# Revit family: R-MMA-480
name_source: partatom
category: Portes
units: mm (PartAtom-declared; Revit-internal decimal feet)

## family parameters
Couper avec des vides une fois chargée = Non
Hôte = Mur
Partagée = Non
Point de calcul de pièce = Oui
Toujours verticalement = Oui

## types (1)
- R-MMA-480
    ----- EQUIPEMENTS ----------------------- = .
    ----- PARAMETRES DE L'HÔTE -------------------- = .
    ----- PARAMETRES DES VANTAUX -------------------- = .
    ----- PARAMETRES POSITION HUISSERIE -------------------- = .
    ----- PARAMETRES PROFIL HUISSERIE -------------------- = .
    ----- TYPE D'HUISSERIE -------------------- = .
    ----- TYPE DE VANTAIL -------------------- = .
    ----PARAMETRES INUTILISES------------------------- = .
    1 Vantail = Oui
    2 Vantaux = Non
    A.E.V = A*4.E*7B.V*C4
    Acoustique = Rw (C ; Ctr) = 43(-1 ;-4)
    Certification = PEFC
    Coloris Oculus = Lauan - Meranti
    Coloris Oculus Métal = Acier - finition peinture thermolaque - gris - brillant
    Coloris Verre Oculus = Verre
    Coloris_Chants = Prépeint
    Construction analytique = <Aucun>
    DAS = Non
    Description = MPC43 COURSIVE - REPRISE DE DOUBLAGE - HB
    Décalage Largeur Paumelle Recouvrement = 0 mm  [stored 0 ft]
    Décalage_Seuil_Vantail = 0 mm  [stored 0 ft]
    Désaffleurement_Vantail = 0 mm  [stored 0 ft]
    Epaisseurs_Vantaux = 58 mm  [stored 0.190289 ft]
    Espacement_Paumelle_Vantail = 0 mm  [stored 0 ft]
    Fabricant = MALERBA
    Ferrage_Encastre = Non
    Fiche Moati = Oui
    Fiche_Produit = MMA-480
    Gabarit_VR = 6
    Hauteur Feuillure Basse Vantail = 18 mm  [stored 0.0590551 ft]
    Hauteur_Axe_Bequille = 1045 mm  [stored 3.42848 ft]
    Hauteur_Vantaux_Souhaitée = 2147 mm  [stored 7.04396 ft]
    Ht Microviseur = 1500 mm  [stored 4.92126 ft]
    Inv_Espacement_Paumelle_Vantail = 5 mm  [stored 0.0164042 ft]
    Inv_Position_Largeur_Paumelle = 0 mm  [stored 0 ft]
    Jeu Profondeur Recouvrement Vantail = 0 mm  [stored 0 ft]
    Jeu_Côté_Articulation_Vantail = 6 mm  [stored 0.019685 ft]
    Jeu_Côté_Fermeture_Vantail = 4 mm  [stored 0.0131234 ft]
    Jeu_Traverse_Basse_Vantail = 8 mm  [stored 0.0262467 ft]
    Jeu_Traverse_Haute_Vantail = 0 mm  [stored 0 ft]
    Largeur Feuillure Battement Articulation = 18 mm  [stored 0.0590551 ft]
    Largeur_Axe_Bequille = 60 mm  [stored 0.19685 ft]
    Largeur_Feuillure_Battement_Semi_Fixe = 18 mm  [stored 0.0590551 ft]
    Largeur_Feuillure_Battement_Service = 18 mm  [stored 0.0590551 ft]
    Largeur_Feuillure_Profil = 18 mm  [stored 0.0590551 ft]
    Largeur_Vantail_Semi_Fixe_Souhaitée = 630 mm  [stored 2.06693 ft]
    Largeur_Vantail_Service_Souhaitée = 960 mm  [stored 3.14961 ft]
    Materiaux_Dominant = Métal
    Microviseur = Non
    Modèle = 43 - SA-HB
    Note d'identification = Bloc-porte métal palier coursive MPC43 1 vantail, simple action, EI30, 43(-1; -4) dB, 1,3 W/m².K, A*4.E*7B.V*C4, stabilité garantie, pour montage reprise de doublage, sur huisserie bois
    Paumelle = Non
    Paumelle_1 = 230 mm  [stored 0.754593 ft]
    Paumelle_2 = 859 mm  [stored 2.81824 ft]
    Paumelle_3 = 859 mm  [stored 2.81824 ft]
    Paumelle_4 = 165 mm
    Pivot_PMT = Non
    Position_Largeur_Paumelle = 0 mm  [stored 0 ft]
    Profondeur Feuillure Basse Vantail = 43 mm  [stored 0.141076 ft]
    Profondeur Feuillure Battement Articulation = 43 mm  [stored 0.141076 ft]
    Profondeur_Feuillure_Battement_Semi_Fixe = 15 mm  [stored 0.0492126 ft]
    Profondeur_Feuillure_Battement_Service = 43 mm  [stored 0.141076 ft]
    Profondeur_Feuillure_Profil = 43 mm  [stored 0.141076 ft]
    Reference_Commerciale = MPC43 EXTERIEUR
    Reprise_Doublage_1 = 30 mm  [stored 0.0984252 ft]
    Reprise_Doublage_2 = 30 mm  [stored 0.0984252 ft]
    Reprise_Doublage_Haut = 30 mm  [stored 0.0984252 ft]
    Resistance_Feu = EI30
    Schéma de simplification = S10
    Sens_Feu = Coté fiches
    Stabilité = Garantie
    Thermique (W/m2.°K) = 1.3
    URL = https://www.malerba.fr
    Vantail à Recouvrement = Oui
    Visibilite_Paum-4 = Oui
    Visibilite_Poignee = Oui
    X_Décalage Hauteur Feuillure Recouvrement = 18 mm  [stored 0.0590551 ft]
    X_Décalage Largeur Feuillure Recouvrement = 36 mm
    X_Décalage Largeur Recouvrement Vantail = 18 mm  [stored 0.0590551 ft]
    X_Décalage Profondeur Recouvrement Vantail = 15 mm  [stored 0.0492126 ft]
    X_Espacement_Paumelle_Vantail = 0 mm  [stored 0 ft]
    X_Fiche Moati = Oui
    X_Inv Décalage Profondeur Recouvrement Vantail = 5 mm  [stored 0.0164042 ft]
    X_Inv_Espacement_Paumelle_Vantail = 5 mm  [stored 0.0164042 ft]
    X_Inv_Position_Largeur_Paumelle = 0 mm  [stored 0 ft]
    X_Paumelle = Non

note: [stored X ft] marks values corroborated as IEEE doubles in the binary element streams (Revit-internal decimal feet)

## geometry (parser evidence)
native form markers: Blend x20
no freeform markers — native parametric forms only
